# Revit family: Shower-Handshower-KOHLER-AWAKEN-K-72421IN
name_source: partatom
category: Plumbing Fixtures
revit_build: Autodesk Revit 2017 (Build: 20160225_1515(x64)
units: mm (PartAtom-declared; Revit-internal decimal feet)

## family parameters
Cut with Voids When Loaded = No
Host = Face
OmniClass Number = 23.31.17.00
OmniClass Title = Showers
Part Type = Normal
Room Calculation Point = No
Round Connector Dimension = Use Diameter
Shared = No

## types (1)
- CP- Polished chrome
    ADA Compliant = No
    Assembly Code = D2010700
    CW Connection = No
    Cold Water Inlet = Cold Water Inlet
    Date Modified = 09/22/2020
    Default Elevation = 0"
    Description = Organic multi-mode handshower with hose
    Drain Included = No
    Finish = Kohler-Metal-CP-Polished_Chrome
    Flow Rate = 0 GPM
    HW Connection = Yes
    Height = 10 3/16"
    Length = 3 3/16"
    Manufacturer = KOHLER Co.
    Master Format 2014 = 22 42 23
    Master Format 2014 Name = Residential Showers
    Material = Metal construction
    Model = K-72421IN-CP
    Pressure = 72.52 psi
    Product Documentation Link = http://resources.kohler.com
    Product Name = AWAKEN
    Product Page URL = https://www.kohler.co.in
    Tempered Water Inlet = Tempered  Water Inlet
    Type = 1
    URL = https://www.kohler.co.in
    Vent Connection = No
    Waste Connection = No
    Waste Water Outlet = Waste Water Outlet
    WaterSense Certified = No
    Width = 4 9/16"

## geometry (parser evidence)
native form markers: Sweep x4
no freeform markers — native parametric forms only
